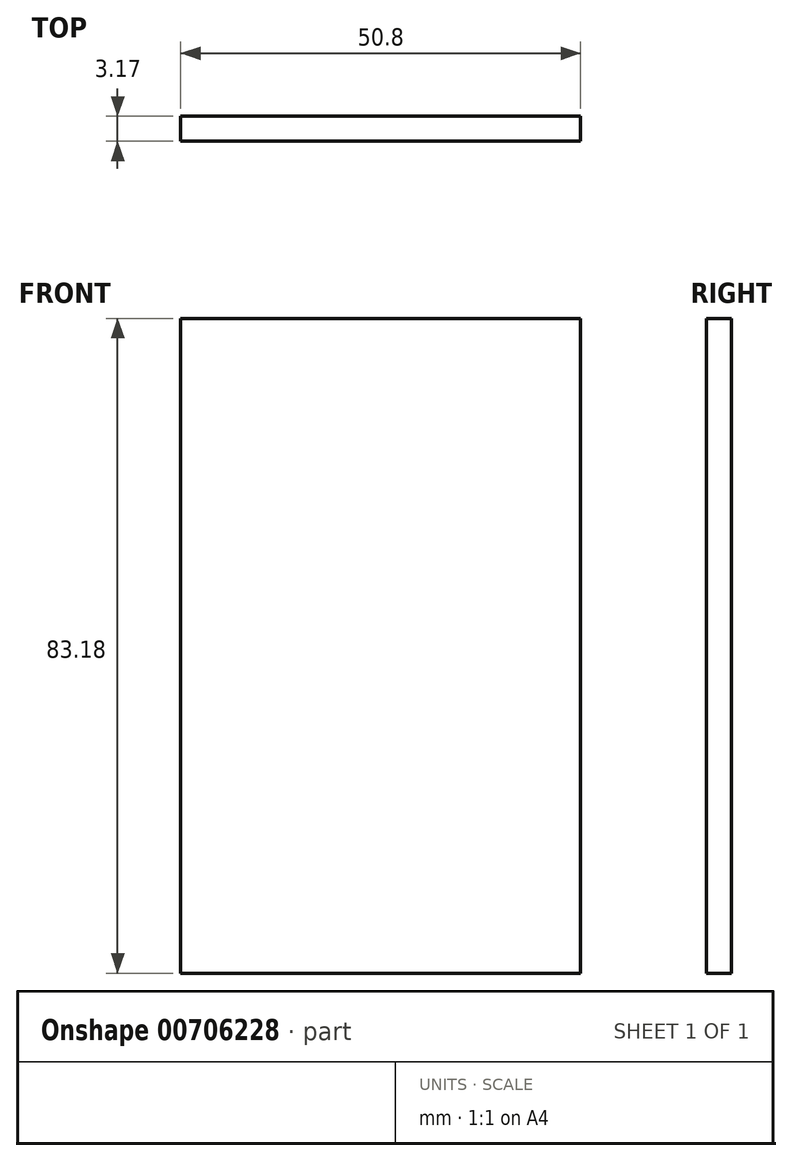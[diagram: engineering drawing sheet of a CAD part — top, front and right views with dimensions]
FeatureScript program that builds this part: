
annotation { "Feature Type Name" : "Feature", "Feature Type Description" : "" }
export const myFeature = defineFeature(function(context is Context, id is Id, definition is map)
    precondition{}
    {
        {
            var Q0;
            Q0=qCreatedBy(makeId("Front.planeOp"),FACE);
            var sketch = newSketch(context, id + "F0", { "sketchPlane" : qUnion([Q0])});
            skLineSegment(sketch, "E0.bottom", {"start": v(-24.5, 51.92) * mm, "end": v(26.3, 51.92) * mm});
            skLineSegment(sketch, "E0.top", {"start": v(-24.5, -31.26) * mm, "end": v(26.3, -31.26) * mm});
            skLineSegment(sketch, "E0.left", {"start": v(-24.5, 51.92) * mm, "end": v(-24.5, -31.26) * mm});
            skLineSegment(sketch, "E0.right", {"start": v(26.3, 51.92) * mm, "end": v(26.3, -31.26) * mm});
            skSolve(sketch);
        }
        {
            var Q0;
            Q0 = qSketchRegion(id + "F0", true);
            extrude(context, id + "F1", {"entities" : qUnion([Q0]), "depth" : 3.17 * mm, "offsetDistance" : 25.4 * mm});
        }
    });
